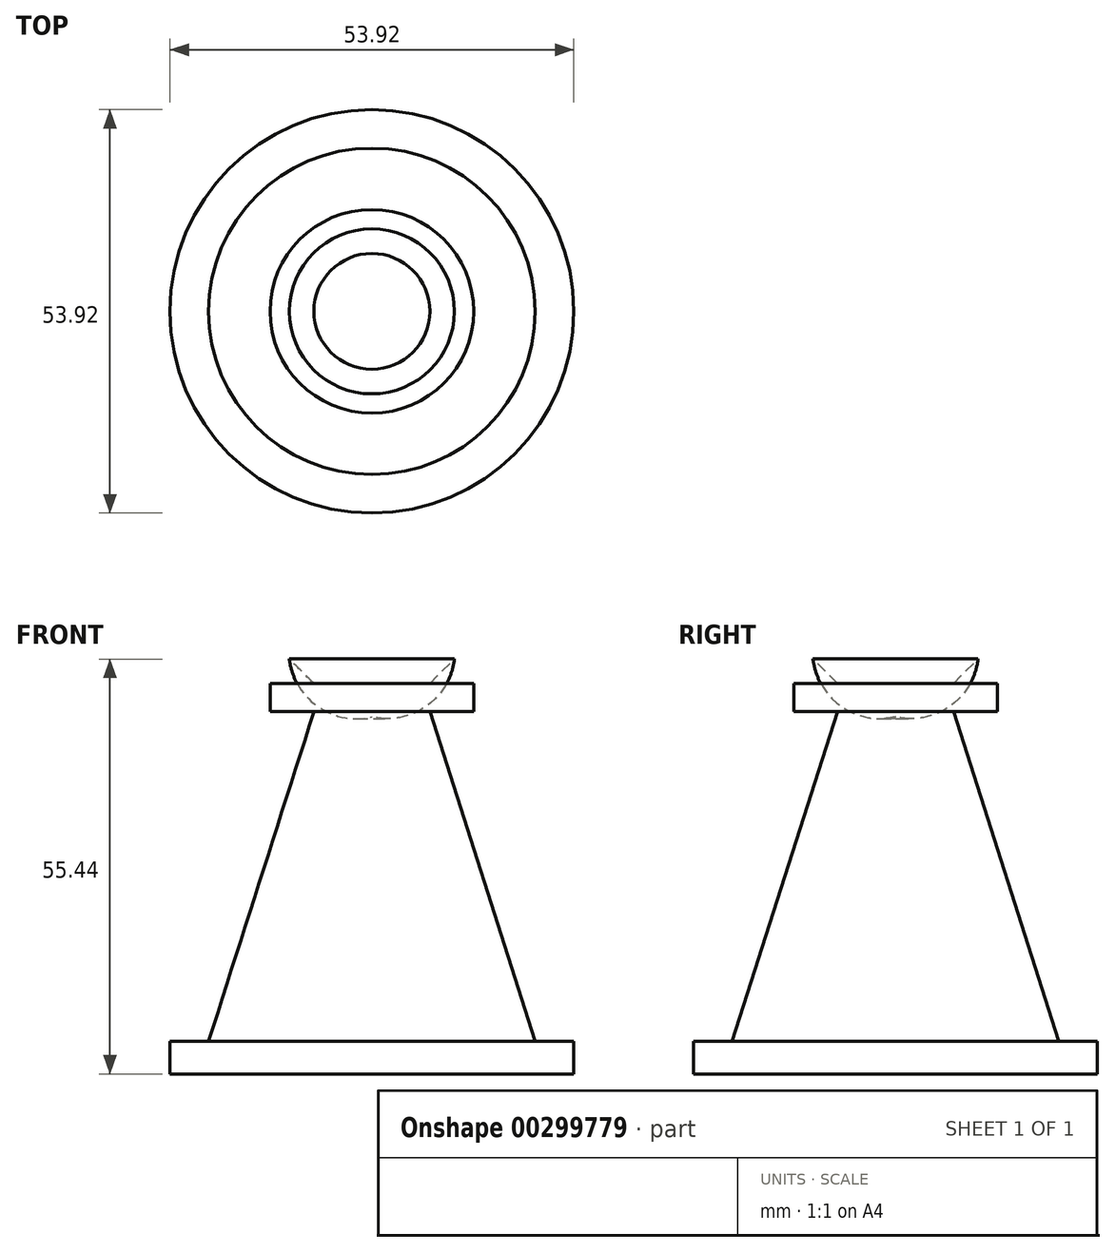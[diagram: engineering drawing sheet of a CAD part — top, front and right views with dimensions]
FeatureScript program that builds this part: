
annotation { "Feature Type Name" : "Feature", "Feature Type Description" : "" }
export const myFeature = defineFeature(function(context is Context, id is Id, definition is map)
    precondition{}
    {
        {
            var Q0;
            Q0=qCreatedBy(makeId("Front.planeOp"),FACE);
            var sketch = newSketch(context, id + "F0", { "sketchPlane" : qUnion([Q0])});
            skLineSegment(sketch, "E0", {"start": v(0, 0) * mm, "end": v(0, 65.29) * mm});
            skArc(sketch, "E1", {"start": v(0, 65.29) * mm, "mid": v(-8.07, 63.23) * mm, "end": v(-11.02, 55.44) * mm});
            skLineSegment(sketch, "E2", {"start": v(-11.02, 55.44) * mm, "end": v(-7.74, 52.16) * mm});
            skLineSegment(sketch, "E3", {"start": v(-7.74, 52.16) * mm, "end": v(-13.6, 52.16) * mm});
            skLineSegment(sketch, "E4", {"start": v(-13.6, 52.16) * mm, "end": v(-13.6, 48.41) * mm});
            skLineSegment(sketch, "E5", {"start": v(-13.6, 48.41) * mm, "end": v(-7.74, 48.41) * mm});
            skLineSegment(sketch, "E6", {"start": v(-7.74, 48.41) * mm, "end": v(-21.8, 4.36) * mm});
            skLineSegment(sketch, "E7", {"start": v(-21.8, 4.36) * mm, "end": v(-26.96, 4.36) * mm});
            skLineSegment(sketch, "E8", {"start": v(-26.96, 4.36) * mm, "end": v(-26.96, 0) * mm});
            skLineSegment(sketch, "E9", {"start": v(-26.96, 0) * mm, "end": v(0, 0) * mm});
            skSolve(sketch);
        }
        {
            var Q0;
            Q0 = qSketchRegion(id + "F0", true);
            var Q1;
            Q1=sQuery(id+"F0.wireOp",EDGE,"E0");
            revolve(context, id + "F1", {"entities" : qUnion([Q0]), "axis" : qUnion([Q1]), "revolveType" : RevolveType.FULL});
        }
    });
